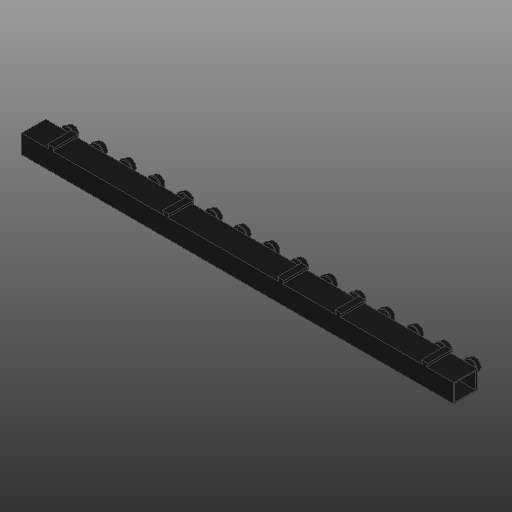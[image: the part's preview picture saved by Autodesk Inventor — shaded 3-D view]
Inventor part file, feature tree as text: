
AUTODESK INVENTOR PART (.ipt)
format: ipt  version: 2020 (Build 240168000, 168)  size: 284,160 bytes
history: native  units: in
note: dims shown in document units (in); Inventor stores cm internally (conversion verified against a paired STEP export)
features: other x6, extrude x3, pattern_linear x1, projected_geometry x1
ambient origin geometry x8: Origin, YZ Plane, XZ Plane, XY Plane, X Axis, Y Axis, Z Axis, Center Point
bodies: Solid1 (feature_tree)
feature tree (11):
  extrude  "Box"  Depth=0.0315in
  other  "Fitting Plane"
  other  "Fitting"
  extrude  "Fitting Entrance"  Depth=0.0157in
  pattern_linear  "Channel Repetition"  Spacing1=0.0157in  [1 undecoded]
  extrude  "Tabs"  Depth=0.4882in TaperAngle=0.0deg
  other  "Box Sketch"
  other  "Fitting Sketch"
  other  "Fitting Entrance Sketch"
  projected_geometry  "Projected Loop1"
  other  "Tab Sketch"
note: 1 required parameter value undecoded (feature->parameter linkage not recoverable at this tier; creation-order binding heuristic only, values carry confidence <= 0.55)
